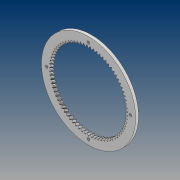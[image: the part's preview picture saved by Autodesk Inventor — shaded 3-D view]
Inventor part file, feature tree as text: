
AUTODESK INVENTOR PART (.ipt)
format: ipt  version: 2021 (Build 250183000, 183)  size: 1,979,392 bytes
history: native  units: mm
features: thread x4, extrude x3, pattern_circular x2, sketch x2, helix x1
ambient origin geometry x8: Origin, YZ Plane, XZ Plane, XY Plane, X Axis, Y Axis, Z Axis, Center Point
bodies: Solid1 (feature_tree)
feature tree (12):
  extrude  "Extrusion1"  Depth=7.936mm
  helix  "Coil1"  [1 undecoded]
  pattern_circular  "Circular Pattern1"  Count=46  [1 undecoded]
  extrude  "Extrusion3"  Depth=10.0mm
  extrude  "Extrusion4"  Depth=10.0mm
  pattern_circular  "Circular Pattern3"  [2 undecoded]
  thread  "Thread5"  [1 undecoded]
  thread  "Thread6"  [1 undecoded]
  thread  "Thread7"  [1 undecoded]
  thread  "Thread8"  [1 undecoded]
  sketch  "Sketch1"  dims[d0=15.872mm d1=0.0mm d2=7.936mm]
  sketch  "Sketch2"  dims[d3=2787.615566mm d4=15.872mm d5=10.0mm d6=0.0mm d7=0.0mm d8=0.0mm d9=0.0mm d10=0.0mm d11=750.0mm d12=0.837758mm d14=460.0mm d15=407.826167mm d16=14.0mm d17=0.0mm d18=230.0mm d24=10.0mm d25=0.0mm d26=0.0mm d27=0.0mm d28=40.0mm d29=360.0deg d39=517.0mm d40=15.872mm d41=0.0mm d42=15.872mm d43=0.0mm d44=15.872mm d45=0.0mm d46=15.872mm d47=0.0mm]
note: 8 required parameter values undecoded (feature->parameter linkage not recoverable at this tier; creation-order binding heuristic only, values carry confidence <= 0.55)
